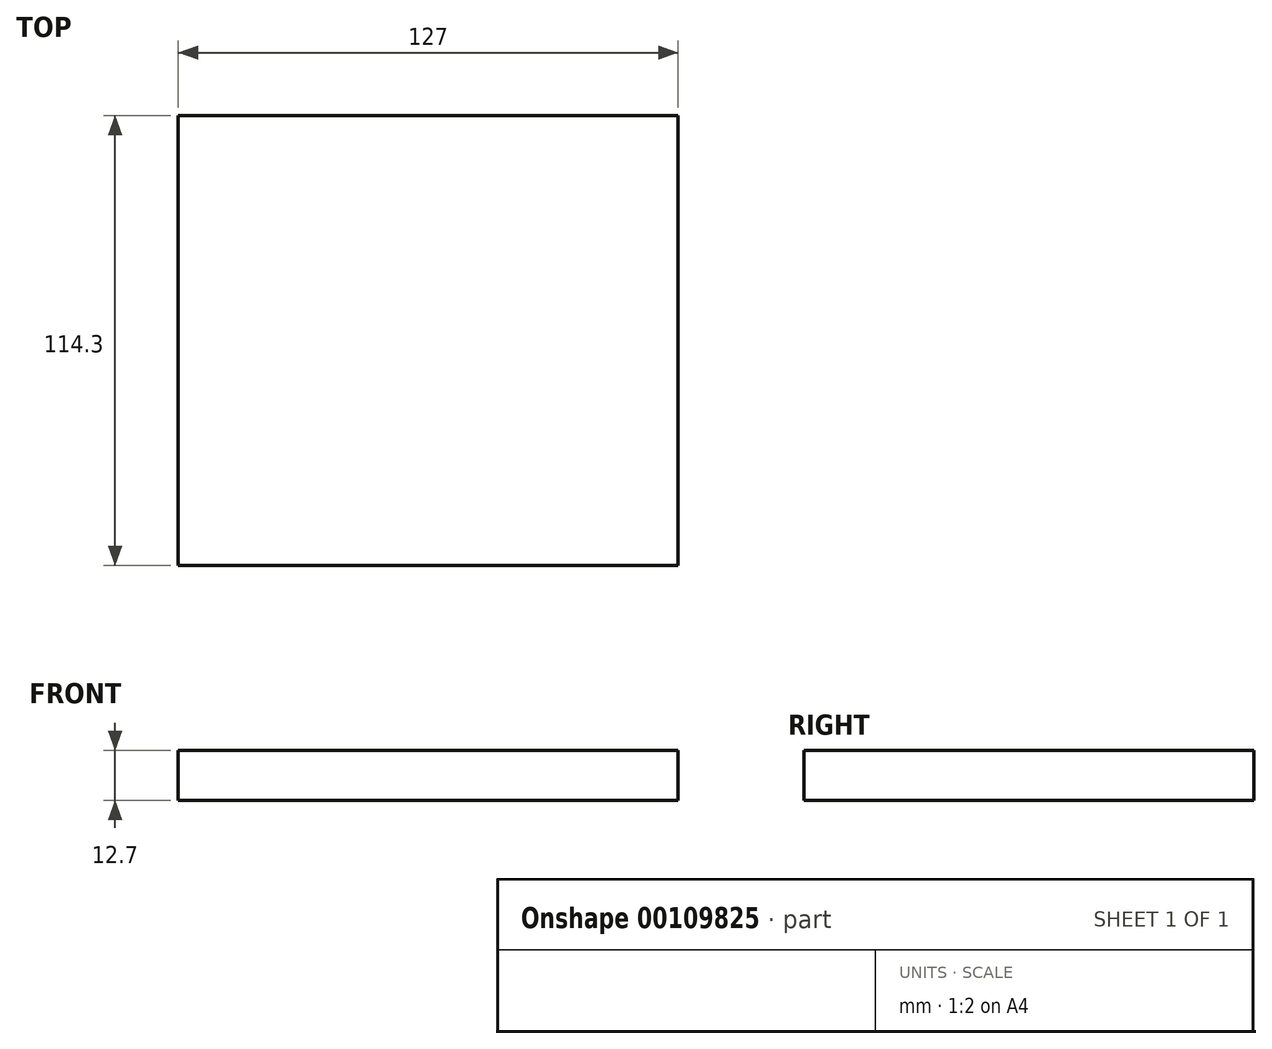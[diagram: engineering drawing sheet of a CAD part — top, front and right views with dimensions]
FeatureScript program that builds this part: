
annotation { "Feature Type Name" : "Feature", "Feature Type Description" : "" }
export const myFeature = defineFeature(function(context is Context, id is Id, definition is map)
    precondition{}
    {
        {
            var Q0;
            Q0=qCreatedBy(makeId("Top.planeOp"),FACE);
            var sketch = newSketch(context, id + "F0", { "sketchPlane" : qUnion([Q0])});
            skLineSegment(sketch, "E0", {"start": v(0, 57.15) * mm, "end": v(63.5, 57.15) * mm});
            skLineSegment(sketch, "E1", {"start": v(63.5, 57.15) * mm, "end": v(63.5, 0) * mm});
            skLineSegment(sketch, "E2.MirrorCS", {"start": v(0, 57.15) * mm, "end": v(-63.5, 57.15) * mm});
            skLineSegment(sketch, "E3.MirrorCS", {"start": v(-63.5, 57.15) * mm, "end": v(-63.5, 0) * mm});
            skLineSegment(sketch, "E4.MirrorCS", {"start": v(-63.5, -57.15) * mm, "end": v(-63.5, 0) * mm});
            skLineSegment(sketch, "E5.MirrorCS", {"start": v(0, -57.15) * mm, "end": v(-63.5, -57.15) * mm});
            skLineSegment(sketch, "E6.MirrorCS", {"start": v(0, -57.15) * mm, "end": v(63.5, -57.15) * mm});
            skLineSegment(sketch, "E7.MirrorCS", {"start": v(63.5, -57.15) * mm, "end": v(63.5, 0) * mm});
            skSolve(sketch);
        }
        {
            var Q0;
            Q0 = qSketchRegion(id + "F0", true);
            extrude(context, id + "F1", {"entities" : qUnion([Q0]), "endBound" : BoundingType.SYMMETRIC, "depth" : 12.7 * mm});
        }
    });
